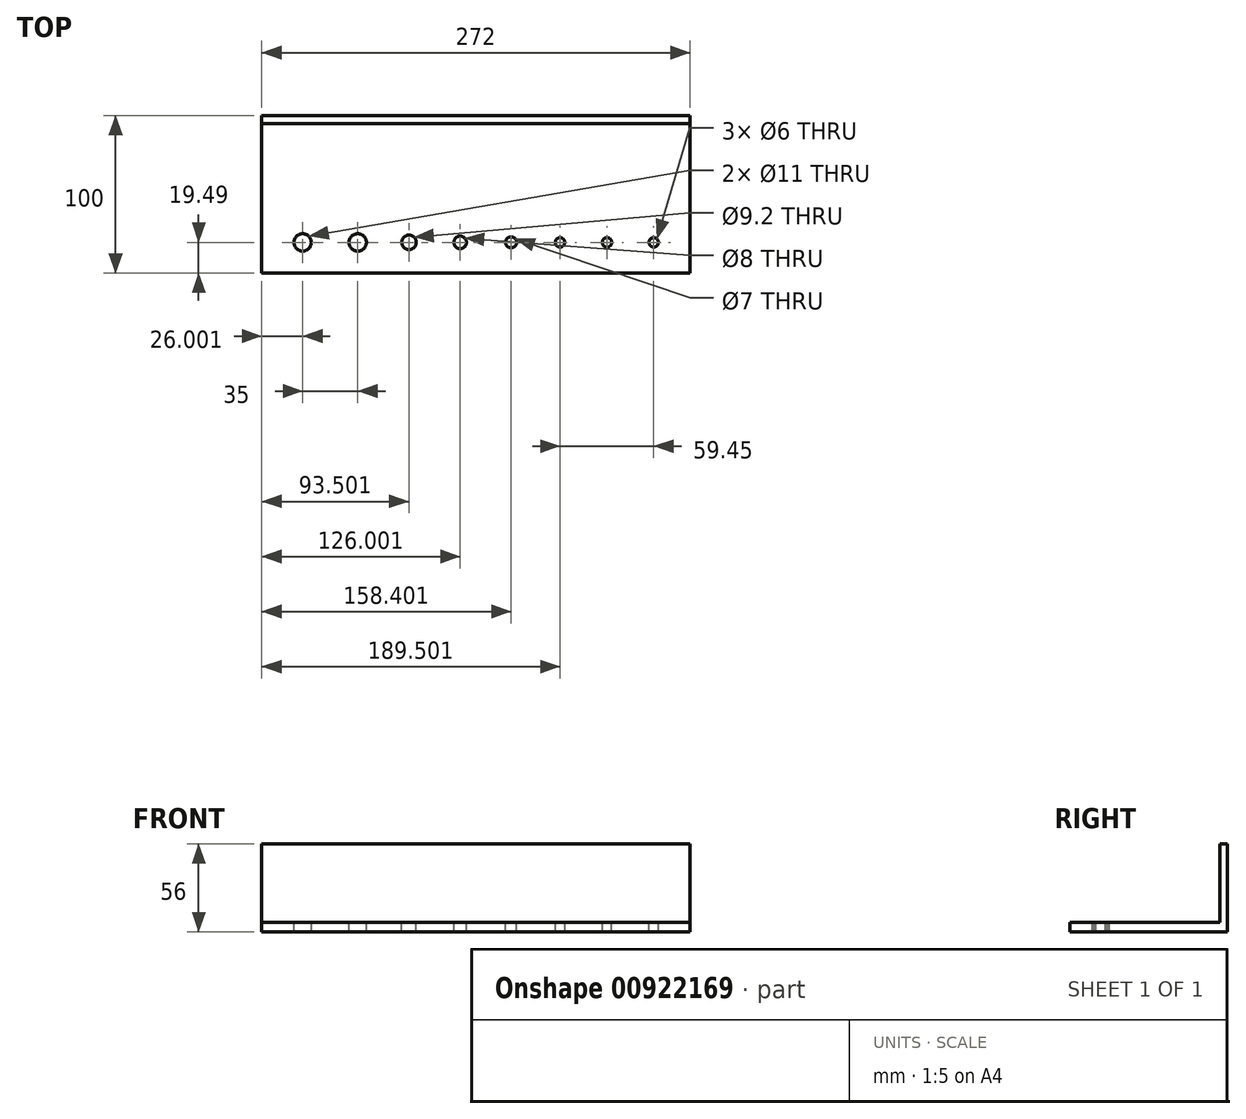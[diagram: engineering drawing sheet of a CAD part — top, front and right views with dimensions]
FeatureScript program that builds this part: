
annotation { "Feature Type Name" : "Feature", "Feature Type Description" : "" }
export const myFeature = defineFeature(function(context is Context, id is Id, definition is map)
    precondition{}
    {
        {
            var Q0;
            Q0=qCreatedBy(makeId("Top.planeOp"),FACE);
            var sketch = newSketch(context, id + "F0", { "sketchPlane" : qUnion([Q0])});
            skLineSegment(sketch, "E0.bottom", {"start": v(-219.95, 30.5) * mm, "end": v(52.05, 30.5) * mm});
            skLineSegment(sketch, "E0.top", {"start": v(-219.95, -19.5) * mm, "end": v(52.05, -19.5) * mm});
            skLineSegment(sketch, "E0.left", {"start": v(-219.95, 30.5) * mm, "end": v(-219.95, -19.5) * mm});
            skLineSegment(sketch, "E0.right", {"start": v(52.05, 30.5) * mm, "end": v(52.05, -19.5) * mm});
            skLineSegment(sketch, "E1", {"start": v(-219.95, 0) * mm, "end": v(52.05, 0) * mm});
            skPoint(sketch, "E1.endSnap0", {"position": v(52.05, 5.5) * mm});
            skPoint(sketch, "E2", {"position": v(-193.95, 0) * mm});
            skPoint(sketch, "E3", {"position": v(-158.95, 0) * mm});
            skPoint(sketch, "E4", {"position": v(-126.45, 0) * mm});
            skPoint(sketch, "E5", {"position": v(-93.95, 0) * mm});
            skPoint(sketch, "E6", {"position": v(-61.55, 0) * mm});
            skPoint(sketch, "E7", {"position": v(-30.45, 0) * mm});
            skPoint(sketch, "E8", {"position": v(-0.65, 0) * mm});
            skPoint(sketch, "E9", {"position": v(29, 0) * mm});
            skSolve(sketch);
        }
        {
            var Q0;
            {var subQ0=sQuery(id+"F0.wireOp",EDGE,"E0.top");Q0=makeQuery(id+"F0.imprint","IMPRINT",FACE,{"disambiguationData":[TD([[makeQuery(id+"F0.imprint","IMPRINT",EDGE,{"derivedFrom":subQ0}),1.0]])]});}
            var Q1;
            {var subQ0=sQuery(id+"F0.wireOp",EDGE,"E0.bottom");Q1=makeQuery(id+"F0.imprint","IMPRINT",FACE,{"disambiguationData":[TD([[makeQuery(id+"F0.imprint","IMPRINT",EDGE,{"derivedFrom":subQ0}),-1.0]])]});}
            extrude(context, id + "F1", {"entities" : qUnion([Q0, Q1]), "oppositeDirection" : true, "depth" : 6 * mm, "offsetDistance" : 25 * mm});
        }
        {
            var Q0;
            Q0=sQuery(id+"F0.wireOp",VERTEX,"E2");
            var Q1;
            Q1=makeQuery(id+"F1.opExtrude","SWEPT_BODY",BODY,{"disambiguationData":[OSD([sQuery(id+"F0.wireOp",EDGE,"E0.bottom"),sQuery(id+"F0.wireOp",EDGE,"E0.top"),sQuery(id+"F0.wireOp",EDGE,"E0.left"),sQuery(id+"F0.wireOp",EDGE,"E0.right")])]});
            hole(context, id + "F2", {"style" : HoleStyle.SIMPLE, "endStyle" : HoleEndStyle.THROUGH, "holeDiameter" : 11 * mm, "majorDiameter" : 5 * mm, "isTappedThrough" : true, "tappedDepth" : 13.5 * mm, "tapClearance" : 3, "locations" : qUnion([Q0]), "scope" : qUnion([Q1])});
        }
        {
            var Q0;
            Q0=sQuery(id+"F0.wireOp",VERTEX,"E3");
            var Q1;
            Q1=makeQuery(id+"F1.opExtrude","SWEPT_BODY",BODY,{"disambiguationData":[OSD([sQuery(id+"F0.wireOp",EDGE,"E0.bottom"),sQuery(id+"F0.wireOp",EDGE,"E0.top"),sQuery(id+"F0.wireOp",EDGE,"E0.left"),sQuery(id+"F0.wireOp",EDGE,"E0.right")])]});
            hole(context, id + "F3", {"style" : HoleStyle.SIMPLE, "endStyle" : HoleEndStyle.THROUGH, "holeDiameter" : 11 * mm, "majorDiameter" : 5 * mm, "isTappedThrough" : true, "tappedDepth" : 13.5 * mm, "tapClearance" : 3, "locations" : qUnion([Q0]), "scope" : qUnion([Q1])});
        }
        {
            var Q0;
            Q0=sQuery(id+"F0.wireOp",VERTEX,"E4");
            var Q1;
            Q1=makeQuery(id+"F1.opExtrude","SWEPT_BODY",BODY,{"disambiguationData":[OSD([sQuery(id+"F0.wireOp",EDGE,"E0.bottom"),sQuery(id+"F0.wireOp",EDGE,"E0.top"),sQuery(id+"F0.wireOp",EDGE,"E0.left"),sQuery(id+"F0.wireOp",EDGE,"E0.right")])]});
            hole(context, id + "F4", {"style" : HoleStyle.SIMPLE, "endStyle" : HoleEndStyle.THROUGH, "holeDiameter" : 9.2 * mm, "majorDiameter" : 5 * mm, "isTappedThrough" : true, "tappedDepth" : 13.5 * mm, "tapClearance" : 3, "locations" : qUnion([Q0]), "scope" : qUnion([Q1])});
        }
        {
            var Q0;
            Q0=sQuery(id+"F0.wireOp",VERTEX,"E5");
            var Q1;
            Q1=makeQuery(id+"F1.opExtrude","SWEPT_BODY",BODY,{"disambiguationData":[OSD([sQuery(id+"F0.wireOp",EDGE,"E0.bottom"),sQuery(id+"F0.wireOp",EDGE,"E0.top"),sQuery(id+"F0.wireOp",EDGE,"E0.left"),sQuery(id+"F0.wireOp",EDGE,"E0.right")])]});
            hole(context, id + "F5", {"style" : HoleStyle.SIMPLE, "endStyle" : HoleEndStyle.THROUGH, "holeDiameter" : 8 * mm, "majorDiameter" : 5 * mm, "isTappedThrough" : true, "tappedDepth" : 13.5 * mm, "tapClearance" : 3, "locations" : qUnion([Q0]), "scope" : qUnion([Q1])});
        }
        {
            var Q0;
            Q0=sQuery(id+"F0.wireOp",VERTEX,"E6");
            var Q1;
            Q1=makeQuery(id+"F1.opExtrude","SWEPT_BODY",BODY,{"disambiguationData":[OSD([sQuery(id+"F0.wireOp",EDGE,"E0.bottom"),sQuery(id+"F0.wireOp",EDGE,"E0.top"),sQuery(id+"F0.wireOp",EDGE,"E0.left"),sQuery(id+"F0.wireOp",EDGE,"E0.right")])]});
            hole(context, id + "F6", {"style" : HoleStyle.SIMPLE, "endStyle" : HoleEndStyle.THROUGH, "holeDiameter" : 7 * mm, "majorDiameter" : 5 * mm, "isTappedThrough" : true, "tappedDepth" : 13.5 * mm, "tapClearance" : 3, "locations" : qUnion([Q0]), "scope" : qUnion([Q1])});
        }
        {
            var Q0;
            Q0=sQuery(id+"F0.wireOp",VERTEX,"E7");
            var Q1;
            Q1=makeQuery(id+"F1.opExtrude","SWEPT_BODY",BODY,{"disambiguationData":[OSD([sQuery(id+"F0.wireOp",EDGE,"E0.bottom"),sQuery(id+"F0.wireOp",EDGE,"E0.top"),sQuery(id+"F0.wireOp",EDGE,"E0.left"),sQuery(id+"F0.wireOp",EDGE,"E0.right")])]});
            hole(context, id + "F7", {"style" : HoleStyle.SIMPLE, "endStyle" : HoleEndStyle.THROUGH, "holeDiameter" : 6 * mm, "majorDiameter" : 5 * mm, "isTappedThrough" : true, "tappedDepth" : 13.5 * mm, "tapClearance" : 3, "locations" : qUnion([Q0]), "scope" : qUnion([Q1])});
        }
        {
            var Q0;
            Q0=sQuery(id+"F0.wireOp",VERTEX,"E9");
            var Q1;
            Q1=makeQuery(id+"F1.opExtrude","SWEPT_BODY",BODY,{"disambiguationData":[OSD([sQuery(id+"F0.wireOp",EDGE,"E0.bottom"),sQuery(id+"F0.wireOp",EDGE,"E0.top"),sQuery(id+"F0.wireOp",EDGE,"E0.left"),sQuery(id+"F0.wireOp",EDGE,"E0.right")])]});
            hole(context, id + "F8", {"style" : HoleStyle.SIMPLE, "endStyle" : HoleEndStyle.THROUGH, "holeDiameter" : 6 * mm, "majorDiameter" : 5 * mm, "isTappedThrough" : true, "tappedDepth" : 13.5 * mm, "tapClearance" : 3, "locations" : qUnion([Q0]), "scope" : qUnion([Q1])});
        }
        {
            var Q0;
            Q0=sQuery(id+"F0.wireOp",VERTEX,"E8");
            var Q1;
            Q1=makeQuery(id+"F1.opExtrude","SWEPT_BODY",BODY,{"disambiguationData":[OSD([sQuery(id+"F0.wireOp",EDGE,"E0.bottom"),sQuery(id+"F0.wireOp",EDGE,"E0.top"),sQuery(id+"F0.wireOp",EDGE,"E0.left"),sQuery(id+"F0.wireOp",EDGE,"E0.right")])]});
            hole(context, id + "F9", {"style" : HoleStyle.SIMPLE, "endStyle" : HoleEndStyle.THROUGH, "holeDiameter" : 6 * mm, "majorDiameter" : 5 * mm, "isTappedThrough" : true, "tappedDepth" : 13.5 * mm, "tapClearance" : 3, "locations" : qUnion([Q0]), "scope" : qUnion([Q1])});
        }
        {
            var Q0;
            Q0=makeQuery(id+"F1.opExtrude","SWEPT_FACE",FACE,{"disambiguationData":[OSD([sQuery(id+"F0.wireOp",EDGE,"E0.bottom")])]});
            extrude(context, id + "F10", {"entities" : qUnion([Q0]), "operationType" : NewBodyOperationType.ADD, "depth" : 50 * mm, "offsetDistance" : 25 * mm});
        }
        {
            var Q0;
            {var subQ0=sQuery(id+"F0.wireOp",EDGE,"E0.bottom");Q0=makeQuery(id+"F0.imprint","IMPRINT",FACE,{"disambiguationData":[TD([[makeQuery(id+"F0.imprint","IMPRINT",EDGE,{"derivedFrom":subQ0}),-1.0]])]});}
            var sketch = newSketch(context, id + "F11", { "sketchPlane" : qUnion([Q0])});
            skLineSegment(sketch, "E10.0.0", {"start": v(-219.95, 80.5) * mm, "end": v(-219.95, -19.5) * mm});
            skLineSegment(sketch, "E10.0.1", {"start": v(-219.95, -19.5) * mm, "end": v(52.05, -19.5) * mm});
            skLineSegment(sketch, "E10.0.2", {"start": v(52.05, -19.5) * mm, "end": v(52.05, 80.5) * mm});
            skLineSegment(sketch, "E10.0.3", {"start": v(52.05, 80.5) * mm, "end": v(-219.95, 80.5) * mm});
            skLineSegment(sketch, "E11", {"start": v(-219.95, 75.5) * mm, "end": v(52.05, 75.5) * mm});
            skSolve(sketch);
        }
        {
            var Q0;
            {var subQ0=sQuery(id+"F11.wireOp",EDGE,"E10.0.3");Q0=makeQuery(id+"F11.imprint","IMPRINT",FACE,{"disambiguationData":[TD([[makeQuery(id+"F11.imprint","IMPRINT",EDGE,{"derivedFrom":subQ0}),1.0]])]});}
            extrude(context, id + "F12", {"entities" : qUnion([Q0]), "operationType" : NewBodyOperationType.ADD, "depth" : 50 * mm, "offsetDistance" : 25 * mm});
        }
    });
